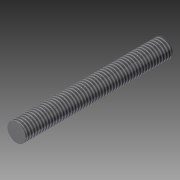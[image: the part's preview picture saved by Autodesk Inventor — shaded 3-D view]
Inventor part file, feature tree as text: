
AUTODESK INVENTOR PART (.ipt)
format: ipt  version: 2014 (Build 180170000, 170)  size: 78,848 bytes
history: native  units: mm
features: extrude x1, thread x1, sketch x1
ambient origin geometry x8: Origin, YZ Plane, XZ Plane, XY Plane, X Axis, Y Axis, Z Axis, Center Point
bodies: Solid1 (feature_tree)
feature tree (3):
  extrude  "Extrusion1"  Depth=40.0mm TaperAngle=0.0deg
  thread  "Thread1"  [1 undecoded]
  sketch  "Sketch1"  dims[d0=5.0mm d1=40.0mm d2=0.0mm d3=10.0mm d4=0.0mm]
note: 1 required parameter value undecoded (feature->parameter linkage not recoverable at this tier; creation-order binding heuristic only, values carry confidence <= 0.55)
